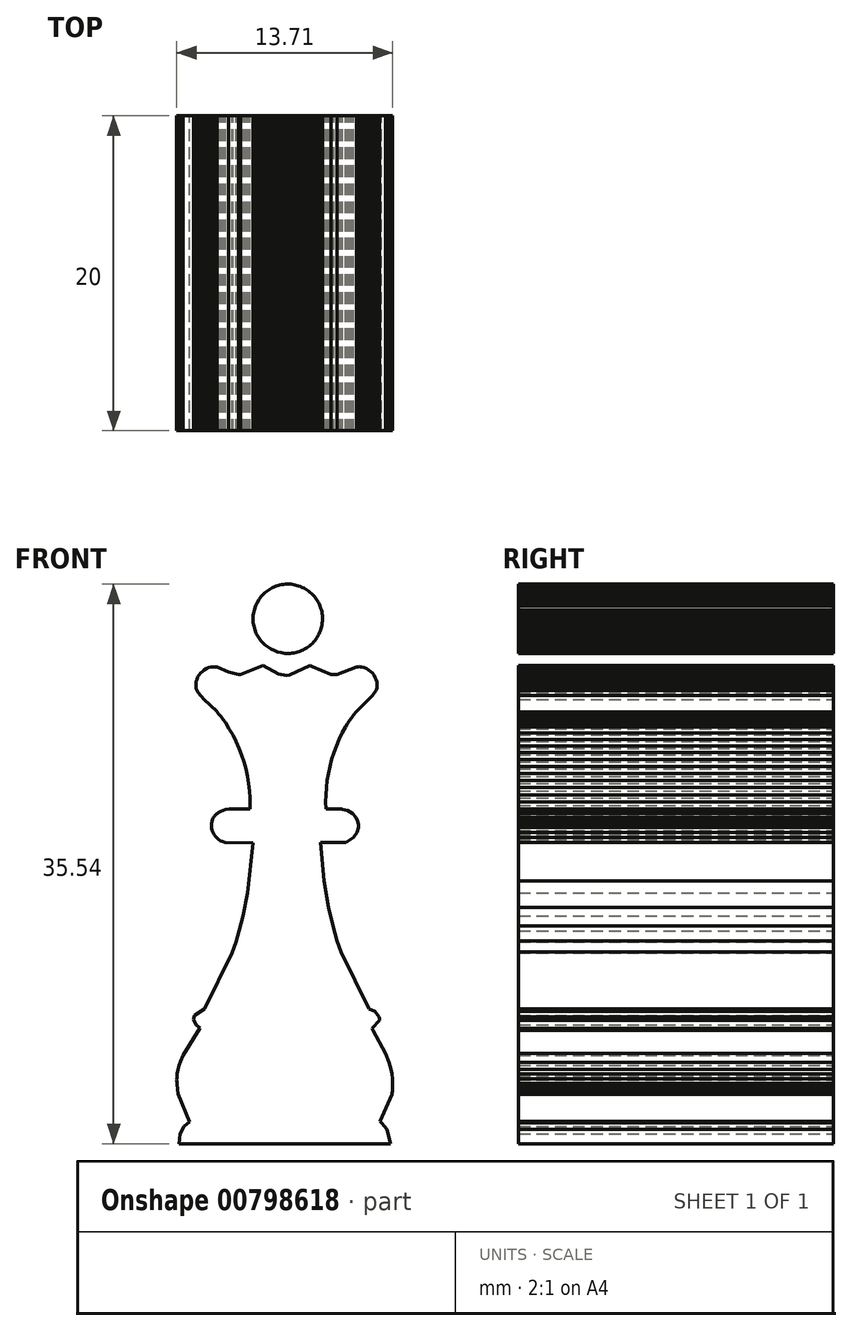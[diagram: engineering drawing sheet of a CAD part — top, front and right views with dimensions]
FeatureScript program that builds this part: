
annotation { "Feature Type Name" : "Feature", "Feature Type Description" : "" }
export const myFeature = defineFeature(function(context is Context, id is Id, definition is map)
    precondition{}
    {
        {
            var Q0;
            Q0=qCreatedBy(makeId("Front.planeOp"),FACE);
            var sketch = newSketch(context, id + "F0", { "sketchPlane" : qUnion([Q0])});
            skLineSegment(sketch, "E0", {"start": v(17.24, 35.4) * mm, "end": v(17.35, 35.45) * mm});
            skLineSegment(sketch, "E1", {"start": v(17.35, 35.45) * mm, "end": v(17.47, 35.48) * mm});
            skLineSegment(sketch, "E2", {"start": v(17.47, 35.48) * mm, "end": v(17.6, 35.51) * mm});
            skLineSegment(sketch, "E3", {"start": v(17.6, 35.51) * mm, "end": v(17.71, 35.53) * mm});
            skLineSegment(sketch, "E4", {"start": v(17.71, 35.53) * mm, "end": v(17.83, 35.54) * mm});
            skLineSegment(sketch, "E5", {"start": v(17.83, 35.54) * mm, "end": v(17.95, 35.54) * mm});
            skLineSegment(sketch, "E6", {"start": v(17.95, 35.54) * mm, "end": v(18.07, 35.54) * mm});
            skLineSegment(sketch, "E7", {"start": v(18.07, 35.54) * mm, "end": v(18.2, 35.53) * mm});
            skLineSegment(sketch, "E8", {"start": v(18.2, 35.53) * mm, "end": v(18.31, 35.52) * mm});
            skLineSegment(sketch, "E9", {"start": v(18.31, 35.52) * mm, "end": v(18.43, 35.5) * mm});
            skLineSegment(sketch, "E10", {"start": v(18.43, 35.5) * mm, "end": v(18.55, 35.46) * mm});
            skLineSegment(sketch, "E11", {"start": v(18.55, 35.46) * mm, "end": v(18.67, 35.43) * mm});
            skLineSegment(sketch, "E12", {"start": v(18.67, 35.43) * mm, "end": v(18.78, 35.39) * mm});
            skLineSegment(sketch, "E13", {"start": v(18.78, 35.39) * mm, "end": v(18.9, 35.34) * mm});
            skLineSegment(sketch, "E14", {"start": v(18.9, 35.34) * mm, "end": v(19, 35.29) * mm});
            skLineSegment(sketch, "E15", {"start": v(19, 35.29) * mm, "end": v(19.1, 35.23) * mm});
            skLineSegment(sketch, "E16", {"start": v(19.1, 35.23) * mm, "end": v(19.21, 35.16) * mm});
            skLineSegment(sketch, "E17", {"start": v(19.21, 35.16) * mm, "end": v(19.31, 35.1) * mm});
            skLineSegment(sketch, "E18", {"start": v(19.31, 35.1) * mm, "end": v(19.4, 35.02) * mm});
            skLineSegment(sketch, "E19", {"start": v(19.4, 35.02) * mm, "end": v(19.5, 34.94) * mm});
            skLineSegment(sketch, "E20", {"start": v(19.5, 34.94) * mm, "end": v(19.58, 34.85) * mm});
            skLineSegment(sketch, "E21", {"start": v(19.58, 34.85) * mm, "end": v(19.67, 34.77) * mm});
            skLineSegment(sketch, "E22", {"start": v(19.67, 34.77) * mm, "end": v(19.74, 34.67) * mm});
            skLineSegment(sketch, "E23", {"start": v(19.74, 34.67) * mm, "end": v(19.81, 34.57) * mm});
            skLineSegment(sketch, "E24", {"start": v(19.81, 34.57) * mm, "end": v(19.88, 34.47) * mm});
            skLineSegment(sketch, "E25", {"start": v(19.88, 34.47) * mm, "end": v(19.94, 34.37) * mm});
            skLineSegment(sketch, "E26", {"start": v(19.94, 34.37) * mm, "end": v(20, 34.26) * mm});
            skLineSegment(sketch, "E27", {"start": v(20, 34.26) * mm, "end": v(20.04, 34.14) * mm});
            skLineSegment(sketch, "E28", {"start": v(20.04, 34.14) * mm, "end": v(20.08, 34.02) * mm});
            skLineSegment(sketch, "E29", {"start": v(20.08, 34.02) * mm, "end": v(20.11, 33.9) * mm});
            skLineSegment(sketch, "E30", {"start": v(20.11, 33.9) * mm, "end": v(20.14, 33.79) * mm});
            skLineSegment(sketch, "E31", {"start": v(20.14, 33.79) * mm, "end": v(20.17, 33.67) * mm});
            skLineSegment(sketch, "E32", {"start": v(20.17, 33.67) * mm, "end": v(20.18, 33.55) * mm});
            skLineSegment(sketch, "E33", {"start": v(20.18, 33.55) * mm, "end": v(20.19, 33.43) * mm});
            skLineSegment(sketch, "E34", {"start": v(20.19, 33.43) * mm, "end": v(20.19, 33.3) * mm});
            skLineSegment(sketch, "E35", {"start": v(20.19, 33.3) * mm, "end": v(20.18, 33.18) * mm});
            skLineSegment(sketch, "E36", {"start": v(20.18, 33.18) * mm, "end": v(20.17, 33.06) * mm});
            skLineSegment(sketch, "E37", {"start": v(20.17, 33.06) * mm, "end": v(20.15, 32.94) * mm});
            skLineSegment(sketch, "E38", {"start": v(20.15, 32.94) * mm, "end": v(20.12, 32.83) * mm});
            skLineSegment(sketch, "E39", {"start": v(20.12, 32.83) * mm, "end": v(20.1, 32.7) * mm});
            skLineSegment(sketch, "E40", {"start": v(20.1, 32.7) * mm, "end": v(20.05, 32.6) * mm});
            skLineSegment(sketch, "E41", {"start": v(20.05, 32.6) * mm, "end": v(20, 32.48) * mm});
            skLineSegment(sketch, "E42", {"start": v(20, 32.48) * mm, "end": v(19.96, 32.37) * mm});
            skLineSegment(sketch, "E43", {"start": v(19.96, 32.37) * mm, "end": v(19.9, 32.26) * mm});
            skLineSegment(sketch, "E44", {"start": v(19.9, 32.26) * mm, "end": v(19.84, 32.16) * mm});
            skLineSegment(sketch, "E45", {"start": v(19.84, 32.16) * mm, "end": v(19.77, 32.06) * mm});
            skLineSegment(sketch, "E46", {"start": v(19.77, 32.06) * mm, "end": v(19.7, 31.96) * mm});
            skLineSegment(sketch, "E47", {"start": v(19.7, 31.96) * mm, "end": v(19.62, 31.87) * mm});
            skLineSegment(sketch, "E48", {"start": v(19.62, 31.87) * mm, "end": v(19.54, 31.78) * mm});
            skLineSegment(sketch, "E49", {"start": v(19.54, 31.78) * mm, "end": v(19.45, 31.7) * mm});
            skLineSegment(sketch, "E50", {"start": v(19.45, 31.7) * mm, "end": v(19.36, 31.62) * mm});
            skLineSegment(sketch, "E51", {"start": v(19.36, 31.62) * mm, "end": v(19.26, 31.54) * mm});
            skLineSegment(sketch, "E52", {"start": v(19.26, 31.54) * mm, "end": v(19.16, 31.48) * mm});
            skLineSegment(sketch, "E53", {"start": v(19.16, 31.48) * mm, "end": v(19.06, 31.42) * mm});
            skLineSegment(sketch, "E54", {"start": v(19.06, 31.42) * mm, "end": v(18.95, 31.36) * mm});
            skLineSegment(sketch, "E55", {"start": v(18.95, 31.36) * mm, "end": v(18.84, 31.31) * mm});
            skLineSegment(sketch, "E56", {"start": v(18.84, 31.31) * mm, "end": v(18.72, 31.27) * mm});
            skLineSegment(sketch, "E57", {"start": v(18.72, 31.27) * mm, "end": v(18.6, 31.23) * mm});
            skLineSegment(sketch, "E58", {"start": v(18.6, 31.23) * mm, "end": v(18.5, 31.2) * mm});
            skLineSegment(sketch, "E59", {"start": v(18.5, 31.2) * mm, "end": v(18.38, 31.18) * mm});
            skLineSegment(sketch, "E60", {"start": v(18.38, 31.18) * mm, "end": v(18.26, 31.16) * mm});
            skLineSegment(sketch, "E61", {"start": v(18.26, 31.16) * mm, "end": v(18.15, 31.15) * mm});
            skLineSegment(sketch, "E62", {"start": v(18.15, 31.15) * mm, "end": v(18.03, 31.14) * mm});
            skLineSegment(sketch, "E63", {"start": v(18.03, 31.14) * mm, "end": v(17.91, 31.14) * mm});
            skLineSegment(sketch, "E64", {"start": v(17.91, 31.14) * mm, "end": v(17.8, 31.15) * mm});
            skLineSegment(sketch, "E65", {"start": v(17.8, 31.15) * mm, "end": v(17.57, 31.18) * mm});
            skLineSegment(sketch, "E66", {"start": v(17.57, 31.18) * mm, "end": v(17.34, 31.24) * mm});
            skLineSegment(sketch, "E67", {"start": v(17.34, 31.24) * mm, "end": v(17.13, 31.32) * mm});
            skLineSegment(sketch, "E68", {"start": v(17.13, 31.32) * mm, "end": v(16.92, 31.42) * mm});
            skLineSegment(sketch, "E69", {"start": v(16.92, 31.42) * mm, "end": v(16.72, 31.54) * mm});
            skLineSegment(sketch, "E70", {"start": v(16.72, 31.54) * mm, "end": v(16.54, 31.69) * mm});
            skLineSegment(sketch, "E71", {"start": v(16.54, 31.69) * mm, "end": v(16.37, 31.85) * mm});
            skLineSegment(sketch, "E72", {"start": v(16.37, 31.85) * mm, "end": v(16.29, 31.93) * mm});
            skLineSegment(sketch, "E73", {"start": v(16.29, 31.93) * mm, "end": v(16.22, 32.02) * mm});
            skLineSegment(sketch, "E74", {"start": v(16.22, 32.02) * mm, "end": v(16.15, 32.12) * mm});
            skLineSegment(sketch, "E75", {"start": v(16.15, 32.12) * mm, "end": v(16.09, 32.21) * mm});
            skLineSegment(sketch, "E76", {"start": v(16.09, 32.21) * mm, "end": v(16.03, 32.31) * mm});
            skLineSegment(sketch, "E77", {"start": v(16.03, 32.31) * mm, "end": v(15.98, 32.42) * mm});
            skLineSegment(sketch, "E78", {"start": v(15.98, 32.42) * mm, "end": v(15.93, 32.53) * mm});
            skLineSegment(sketch, "E79", {"start": v(15.93, 32.53) * mm, "end": v(15.9, 32.64) * mm});
            skLineSegment(sketch, "E80", {"start": v(15.9, 32.64) * mm, "end": v(15.86, 32.75) * mm});
            skLineSegment(sketch, "E81", {"start": v(15.86, 32.75) * mm, "end": v(15.83, 32.87) * mm});
            skLineSegment(sketch, "E82", {"start": v(15.83, 32.87) * mm, "end": v(15.8, 32.98) * mm});
            skLineSegment(sketch, "E83", {"start": v(15.8, 32.98) * mm, "end": v(15.79, 33.1) * mm});
            skLineSegment(sketch, "E84", {"start": v(15.79, 33.1) * mm, "end": v(15.78, 33.22) * mm});
            skLineSegment(sketch, "E85", {"start": v(15.78, 33.22) * mm, "end": v(15.77, 33.34) * mm});
            skLineSegment(sketch, "E86", {"start": v(15.77, 33.34) * mm, "end": v(15.78, 33.45) * mm});
            skLineSegment(sketch, "E87", {"start": v(15.78, 33.45) * mm, "end": v(15.79, 33.57) * mm});
            skLineSegment(sketch, "E88", {"start": v(15.79, 33.57) * mm, "end": v(15.8, 33.68) * mm});
            skLineSegment(sketch, "E89", {"start": v(15.8, 33.68) * mm, "end": v(15.86, 33.91) * mm});
            skLineSegment(sketch, "E90", {"start": v(15.86, 33.91) * mm, "end": v(15.93, 34.14) * mm});
            skLineSegment(sketch, "E91", {"start": v(15.93, 34.14) * mm, "end": v(16.03, 34.35) * mm});
            skLineSegment(sketch, "E92", {"start": v(16.03, 34.35) * mm, "end": v(16.15, 34.55) * mm});
            skLineSegment(sketch, "E93", {"start": v(16.15, 34.55) * mm, "end": v(16.29, 34.74) * mm});
            skLineSegment(sketch, "E94", {"start": v(16.29, 34.74) * mm, "end": v(16.44, 34.91) * mm});
            skLineSegment(sketch, "E95", {"start": v(16.44, 34.91) * mm, "end": v(16.53, 35) * mm});
            skLineSegment(sketch, "E96", {"start": v(16.53, 35) * mm, "end": v(16.62, 35.07) * mm});
            skLineSegment(sketch, "E97", {"start": v(16.62, 35.07) * mm, "end": v(16.71, 35.14) * mm});
            skLineSegment(sketch, "E98", {"start": v(16.71, 35.14) * mm, "end": v(16.81, 35.2) * mm});
            skLineSegment(sketch, "E99", {"start": v(16.81, 35.2) * mm, "end": v(16.91, 35.27) * mm});
            skLineSegment(sketch, "E100", {"start": v(16.91, 35.27) * mm, "end": v(17.02, 35.32) * mm});
            skLineSegment(sketch, "E101", {"start": v(17.02, 35.32) * mm, "end": v(17.12, 35.37) * mm});
            skLineSegment(sketch, "E102", {"start": v(17.12, 35.37) * mm, "end": v(17.24, 35.4) * mm});
            skLineSegment(sketch, "E103", {"start": v(12.17, 28.9) * mm, "end": v(12.15, 28.97) * mm});
            skLineSegment(sketch, "E104", {"start": v(12.15, 28.97) * mm, "end": v(12.14, 29.05) * mm});
            skLineSegment(sketch, "E105", {"start": v(12.14, 29.05) * mm, "end": v(12.14, 29.2) * mm});
            skLineSegment(sketch, "E106", {"start": v(12.14, 29.2) * mm, "end": v(12.16, 29.35) * mm});
            skLineSegment(sketch, "E107", {"start": v(12.16, 29.35) * mm, "end": v(12.2, 29.5) * mm});
            skLineSegment(sketch, "E108", {"start": v(12.2, 29.5) * mm, "end": v(12.27, 29.64) * mm});
            skLineSegment(sketch, "E109", {"start": v(12.27, 29.64) * mm, "end": v(12.35, 29.77) * mm});
            skLineSegment(sketch, "E110", {"start": v(12.35, 29.77) * mm, "end": v(12.44, 29.9) * mm});
            skLineSegment(sketch, "E111", {"start": v(12.44, 29.9) * mm, "end": v(12.55, 30) * mm});
            skLineSegment(sketch, "E112", {"start": v(12.55, 30) * mm, "end": v(12.68, 30.1) * mm});
            skLineSegment(sketch, "E113", {"start": v(12.68, 30.1) * mm, "end": v(12.8, 30.17) * mm});
            skLineSegment(sketch, "E114", {"start": v(12.8, 30.17) * mm, "end": v(12.95, 30.23) * mm});
            skLineSegment(sketch, "E115", {"start": v(12.95, 30.23) * mm, "end": v(13.1, 30.27) * mm});
            skLineSegment(sketch, "E116", {"start": v(13.1, 30.27) * mm, "end": v(13.25, 30.3) * mm});
            skLineSegment(sketch, "E117", {"start": v(13.25, 30.3) * mm, "end": v(13.4, 30.29) * mm});
            skLineSegment(sketch, "E118", {"start": v(13.4, 30.29) * mm, "end": v(13.48, 30.28) * mm});
            skLineSegment(sketch, "E119", {"start": v(13.48, 30.28) * mm, "end": v(14.23, 29.95) * mm});
            skLineSegment(sketch, "E120", {"start": v(14.23, 29.95) * mm, "end": v(14.87, 29.8) * mm});
            skLineSegment(sketch, "E121", {"start": v(14.87, 29.8) * mm, "end": v(14.98, 29.8) * mm});
            skLineSegment(sketch, "E122", {"start": v(14.98, 29.8) * mm, "end": v(16.4, 30.37) * mm});
            skLineSegment(sketch, "E123", {"start": v(16.4, 30.37) * mm, "end": v(17.4, 29.82) * mm});
            skLineSegment(sketch, "E124", {"start": v(17.4, 29.82) * mm, "end": v(17.91, 29.75) * mm});
            skLineSegment(sketch, "E125", {"start": v(17.91, 29.75) * mm, "end": v(18.08, 29.76) * mm});
            skLineSegment(sketch, "E126", {"start": v(18.08, 29.76) * mm, "end": v(19.4, 30.37) * mm});
            skLineSegment(sketch, "E127", {"start": v(19.4, 30.37) * mm, "end": v(19.51, 30.3) * mm});
            skLineSegment(sketch, "E128", {"start": v(19.51, 30.3) * mm, "end": v(20.72, 29.8) * mm});
            skLineSegment(sketch, "E129", {"start": v(20.72, 29.8) * mm, "end": v(21.1, 29.81) * mm});
            skLineSegment(sketch, "E130", {"start": v(21.1, 29.81) * mm, "end": v(22.36, 30.28) * mm});
            skLineSegment(sketch, "E131", {"start": v(22.36, 30.28) * mm, "end": v(22.44, 30.3) * mm});
            skLineSegment(sketch, "E132", {"start": v(22.44, 30.3) * mm, "end": v(22.52, 30.3) * mm});
            skLineSegment(sketch, "E133", {"start": v(22.52, 30.3) * mm, "end": v(22.6, 30.29) * mm});
            skLineSegment(sketch, "E134", {"start": v(22.6, 30.29) * mm, "end": v(22.68, 30.28) * mm});
            skLineSegment(sketch, "E135", {"start": v(22.68, 30.28) * mm, "end": v(22.83, 30.24) * mm});
            skLineSegment(sketch, "E136", {"start": v(22.83, 30.24) * mm, "end": v(22.97, 30.18) * mm});
            skLineSegment(sketch, "E137", {"start": v(22.97, 30.18) * mm, "end": v(23.11, 30.1) * mm});
            skLineSegment(sketch, "E138", {"start": v(23.11, 30.1) * mm, "end": v(23.24, 30) * mm});
            skLineSegment(sketch, "E139", {"start": v(23.24, 30) * mm, "end": v(23.35, 29.89) * mm});
            skLineSegment(sketch, "E140", {"start": v(23.35, 29.89) * mm, "end": v(23.45, 29.76) * mm});
            skLineSegment(sketch, "E141", {"start": v(23.45, 29.76) * mm, "end": v(23.53, 29.63) * mm});
            skLineSegment(sketch, "E142", {"start": v(23.53, 29.63) * mm, "end": v(23.6, 29.48) * mm});
            skLineSegment(sketch, "E143", {"start": v(23.6, 29.48) * mm, "end": v(23.63, 29.33) * mm});
            skLineSegment(sketch, "E144", {"start": v(23.63, 29.33) * mm, "end": v(23.65, 29.18) * mm});
            skLineSegment(sketch, "E145", {"start": v(23.65, 29.18) * mm, "end": v(23.65, 29.1) * mm});
            skLineSegment(sketch, "E146", {"start": v(23.65, 29.1) * mm, "end": v(23.65, 29.02) * mm});
            skLineSegment(sketch, "E147", {"start": v(23.65, 29.02) * mm, "end": v(23.63, 28.94) * mm});
            skLineSegment(sketch, "E148", {"start": v(23.63, 28.94) * mm, "end": v(23.61, 28.86) * mm});
            skLineSegment(sketch, "E149", {"start": v(23.61, 28.86) * mm, "end": v(23.59, 28.79) * mm});
            skLineSegment(sketch, "E150", {"start": v(23.59, 28.79) * mm, "end": v(23.38, 28.46) * mm});
            skLineSegment(sketch, "E151", {"start": v(23.38, 28.46) * mm, "end": v(22.3, 27.42) * mm});
            skLineSegment(sketch, "E152", {"start": v(22.3, 27.42) * mm, "end": v(22.17, 27.24) * mm});
            skLineSegment(sketch, "E153", {"start": v(22.17, 27.24) * mm, "end": v(22.03, 27.05) * mm});
            skLineSegment(sketch, "E154", {"start": v(22.03, 27.05) * mm, "end": v(21.9, 26.87) * mm});
            skLineSegment(sketch, "E155", {"start": v(21.9, 26.87) * mm, "end": v(21.78, 26.68) * mm});
            skLineSegment(sketch, "E156", {"start": v(21.78, 26.68) * mm, "end": v(21.66, 26.48) * mm});
            skLineSegment(sketch, "E157", {"start": v(21.66, 26.48) * mm, "end": v(21.44, 26.08) * mm});
            skLineSegment(sketch, "E158", {"start": v(21.44, 26.08) * mm, "end": v(21.24, 25.68) * mm});
            skLineSegment(sketch, "E159", {"start": v(21.24, 25.68) * mm, "end": v(21.06, 25.26) * mm});
            skLineSegment(sketch, "E160", {"start": v(21.06, 25.26) * mm, "end": v(20.9, 24.83) * mm});
            skLineSegment(sketch, "E161", {"start": v(20.9, 24.83) * mm, "end": v(20.77, 24.4) * mm});
            skLineSegment(sketch, "E162", {"start": v(20.77, 24.4) * mm, "end": v(20.65, 23.96) * mm});
            skLineSegment(sketch, "E163", {"start": v(20.65, 23.96) * mm, "end": v(20.56, 23.51) * mm});
            skLineSegment(sketch, "E164", {"start": v(20.56, 23.51) * mm, "end": v(20.49, 23.06) * mm});
            skLineSegment(sketch, "E165", {"start": v(20.49, 23.06) * mm, "end": v(20.43, 22.61) * mm});
            skLineSegment(sketch, "E166", {"start": v(20.43, 22.61) * mm, "end": v(20.4, 22.16) * mm});
            skLineSegment(sketch, "E167", {"start": v(20.4, 22.16) * mm, "end": v(20.4, 21.7) * mm});
            skLineSegment(sketch, "E168", {"start": v(20.4, 21.7) * mm, "end": v(20.4, 21.25) * mm});
            skLineSegment(sketch, "E169", {"start": v(20.4, 21.25) * mm, "end": v(21.4, 21.25) * mm});
            skLineSegment(sketch, "E170", {"start": v(21.4, 21.25) * mm, "end": v(21.46, 21.24) * mm});
            skLineSegment(sketch, "E171", {"start": v(21.46, 21.24) * mm, "end": v(21.77, 21.17) * mm});
            skLineSegment(sketch, "E172", {"start": v(21.77, 21.17) * mm, "end": v(22.1, 20.97) * mm});
            skLineSegment(sketch, "E173", {"start": v(22.1, 20.97) * mm, "end": v(22.3, 20.73) * mm});
            skLineSegment(sketch, "E174", {"start": v(22.3, 20.73) * mm, "end": v(22.42, 20.49) * mm});
            skLineSegment(sketch, "E175", {"start": v(22.42, 20.49) * mm, "end": v(22.46, 20.28) * mm});
            skLineSegment(sketch, "E176", {"start": v(22.46, 20.28) * mm, "end": v(22.46, 20.07) * mm});
            skLineSegment(sketch, "E177", {"start": v(22.46, 20.07) * mm, "end": v(22.38, 19.78) * mm});
            skLineSegment(sketch, "E178", {"start": v(22.38, 19.78) * mm, "end": v(22.15, 19.45) * mm});
            skLineSegment(sketch, "E179", {"start": v(22.15, 19.45) * mm, "end": v(21.69, 19.15) * mm});
            skLineSegment(sketch, "E180", {"start": v(21.69, 19.15) * mm, "end": v(20.06, 19.13) * mm});
            skLineSegment(sketch, "E181", {"start": v(20.06, 19.13) * mm, "end": v(20.29, 16.7) * mm});
            skLineSegment(sketch, "E182", {"start": v(20.29, 16.7) * mm, "end": v(20.56, 15) * mm});
            skLineSegment(sketch, "E183", {"start": v(20.56, 15) * mm, "end": v(20.84, 13.82) * mm});
            skLineSegment(sketch, "E184", {"start": v(20.84, 13.82) * mm, "end": v(21.12, 12.88) * mm});
            skLineSegment(sketch, "E185", {"start": v(21.12, 12.88) * mm, "end": v(21.37, 12.19) * mm});
            skLineSegment(sketch, "E186", {"start": v(21.37, 12.19) * mm, "end": v(23.13, 8.56) * mm});
            skLineSegment(sketch, "E187", {"start": v(23.13, 8.56) * mm, "end": v(23.52, 8.4) * mm});
            skLineSegment(sketch, "E188", {"start": v(23.52, 8.4) * mm, "end": v(23.79, 8.04) * mm});
            skLineSegment(sketch, "E189", {"start": v(23.79, 8.04) * mm, "end": v(23.8, 7.97) * mm});
            skLineSegment(sketch, "E190", {"start": v(23.8, 7.97) * mm, "end": v(23.8, 7.82) * mm});
            skLineSegment(sketch, "E191", {"start": v(23.8, 7.82) * mm, "end": v(23.33, 7.34) * mm});
            skLineSegment(sketch, "E192", {"start": v(23.33, 7.34) * mm, "end": v(23.4, 7.2) * mm});
            skLineSegment(sketch, "E193", {"start": v(23.4, 7.2) * mm, "end": v(24.2, 5.72) * mm});
            skLineSegment(sketch, "E194", {"start": v(24.2, 5.72) * mm, "end": v(24.4, 5.15) * mm});
            skLineSegment(sketch, "E195", {"start": v(24.4, 5.15) * mm, "end": v(24.53, 4.71) * mm});
            skLineSegment(sketch, "E196", {"start": v(24.53, 4.71) * mm, "end": v(24.59, 4.42) * mm});
            skLineSegment(sketch, "E197", {"start": v(24.59, 4.42) * mm, "end": v(24.63, 4.12) * mm});
            skLineSegment(sketch, "E198", {"start": v(24.63, 4.12) * mm, "end": v(24.64, 3.82) * mm});
            skLineSegment(sketch, "E199", {"start": v(24.64, 3.82) * mm, "end": v(24.64, 3.66) * mm});
            skLineSegment(sketch, "E200", {"start": v(24.64, 3.66) * mm, "end": v(24.63, 3.5) * mm});
            skLineSegment(sketch, "E201", {"start": v(24.63, 3.5) * mm, "end": v(24.62, 3.35) * mm});
            skLineSegment(sketch, "E202", {"start": v(24.62, 3.35) * mm, "end": v(24.6, 3.2) * mm});
            skLineSegment(sketch, "E203", {"start": v(24.6, 3.2) * mm, "end": v(24.6, 3.13) * mm});
            skLineSegment(sketch, "E204", {"start": v(24.6, 3.13) * mm, "end": v(23.85, 1.4) * mm});
            skLineSegment(sketch, "E205", {"start": v(23.85, 1.4) * mm, "end": v(23.94, 1.33) * mm});
            skLineSegment(sketch, "E206", {"start": v(23.94, 1.33) * mm, "end": v(24.28, 0.9) * mm});
            skLineSegment(sketch, "E207", {"start": v(24.28, 0.9) * mm, "end": v(24.5, 0) * mm});
            skLineSegment(sketch, "E208", {"start": v(24.5, 0) * mm, "end": v(11.06, 0) * mm});
            skLineSegment(sketch, "E209", {"start": v(11.06, 0) * mm, "end": v(11.14, 0.6) * mm});
            skLineSegment(sketch, "E210", {"start": v(11.14, 0.6) * mm, "end": v(11.4, 1.09) * mm});
            skLineSegment(sketch, "E211", {"start": v(11.4, 1.09) * mm, "end": v(11.73, 1.39) * mm});
            skLineSegment(sketch, "E212", {"start": v(11.73, 1.39) * mm, "end": v(11, 3.15) * mm});
            skLineSegment(sketch, "E213", {"start": v(11, 3.15) * mm, "end": v(10.95, 3.76) * mm});
            skLineSegment(sketch, "E214", {"start": v(10.95, 3.76) * mm, "end": v(10.94, 3.9) * mm});
            skLineSegment(sketch, "E215", {"start": v(10.94, 3.9) * mm, "end": v(10.93, 4.04) * mm});
            skLineSegment(sketch, "E216", {"start": v(10.93, 4.04) * mm, "end": v(10.94, 4.18) * mm});
            skLineSegment(sketch, "E217", {"start": v(10.94, 4.18) * mm, "end": v(10.95, 4.31) * mm});
            skLineSegment(sketch, "E218", {"start": v(10.95, 4.31) * mm, "end": v(10.96, 4.45) * mm});
            skLineSegment(sketch, "E219", {"start": v(10.96, 4.45) * mm, "end": v(11.02, 4.7) * mm});
            skLineSegment(sketch, "E220", {"start": v(11.02, 4.7) * mm, "end": v(11.09, 4.97) * mm});
            skLineSegment(sketch, "E221", {"start": v(11.09, 4.97) * mm, "end": v(11.18, 5.22) * mm});
            skLineSegment(sketch, "E222", {"start": v(11.18, 5.22) * mm, "end": v(11.35, 5.6) * mm});
            skLineSegment(sketch, "E223", {"start": v(11.35, 5.6) * mm, "end": v(12.4, 7.36) * mm});
            skLineSegment(sketch, "E224", {"start": v(12.4, 7.36) * mm, "end": v(12.17, 7.55) * mm});
            skLineSegment(sketch, "E225", {"start": v(12.17, 7.55) * mm, "end": v(11.98, 7.9) * mm});
            skLineSegment(sketch, "E226", {"start": v(11.98, 7.9) * mm, "end": v(12.02, 8.05) * mm});
            skLineSegment(sketch, "E227", {"start": v(12.02, 8.05) * mm, "end": v(12.05, 8.15) * mm});
            skLineSegment(sketch, "E228", {"start": v(12.05, 8.15) * mm, "end": v(12.7, 8.56) * mm});
            skLineSegment(sketch, "E229", {"start": v(12.7, 8.56) * mm, "end": v(14.43, 12.1) * mm});
            skLineSegment(sketch, "E230", {"start": v(14.43, 12.1) * mm, "end": v(14.68, 12.8) * mm});
            skLineSegment(sketch, "E231", {"start": v(14.68, 12.8) * mm, "end": v(14.9, 13.51) * mm});
            skLineSegment(sketch, "E232", {"start": v(14.9, 13.51) * mm, "end": v(15.14, 14.46) * mm});
            skLineSegment(sketch, "E233", {"start": v(15.14, 14.46) * mm, "end": v(15.42, 15.92) * mm});
            skLineSegment(sketch, "E234", {"start": v(15.42, 15.92) * mm, "end": v(15.77, 19.1) * mm});
            skLineSegment(sketch, "E235", {"start": v(15.77, 19.1) * mm, "end": v(14, 19.14) * mm});
            skLineSegment(sketch, "E236", {"start": v(14, 19.14) * mm, "end": v(13.85, 19.18) * mm});
            skLineSegment(sketch, "E237", {"start": v(13.85, 19.18) * mm, "end": v(13.72, 19.24) * mm});
            skLineSegment(sketch, "E238", {"start": v(13.72, 19.24) * mm, "end": v(13.6, 19.32) * mm});
            skLineSegment(sketch, "E239", {"start": v(13.6, 19.32) * mm, "end": v(13.48, 19.41) * mm});
            skLineSegment(sketch, "E240", {"start": v(13.48, 19.41) * mm, "end": v(13.38, 19.52) * mm});
            skLineSegment(sketch, "E241", {"start": v(13.38, 19.52) * mm, "end": v(13.3, 19.64) * mm});
            skLineSegment(sketch, "E242", {"start": v(13.3, 19.64) * mm, "end": v(13.23, 19.77) * mm});
            skLineSegment(sketch, "E243", {"start": v(13.23, 19.77) * mm, "end": v(13.18, 19.9) * mm});
            skLineSegment(sketch, "E244", {"start": v(13.18, 19.9) * mm, "end": v(13.14, 20.05) * mm});
            skLineSegment(sketch, "E245", {"start": v(13.14, 20.05) * mm, "end": v(13.13, 20.2) * mm});
            skLineSegment(sketch, "E246", {"start": v(13.13, 20.2) * mm, "end": v(13.13, 20.33) * mm});
            skLineSegment(sketch, "E247", {"start": v(13.13, 20.33) * mm, "end": v(13.16, 20.48) * mm});
            skLineSegment(sketch, "E248", {"start": v(13.16, 20.48) * mm, "end": v(13.22, 20.61) * mm});
            skLineSegment(sketch, "E249", {"start": v(13.22, 20.61) * mm, "end": v(13.25, 20.68) * mm});
            skLineSegment(sketch, "E250", {"start": v(13.25, 20.68) * mm, "end": v(13.3, 20.74) * mm});
            skLineSegment(sketch, "E251", {"start": v(13.3, 20.74) * mm, "end": v(13.34, 20.8) * mm});
            skLineSegment(sketch, "E252", {"start": v(13.34, 20.8) * mm, "end": v(13.4, 20.87) * mm});
            skLineSegment(sketch, "E253", {"start": v(13.4, 20.87) * mm, "end": v(13.46, 20.93) * mm});
            skLineSegment(sketch, "E254", {"start": v(13.46, 20.93) * mm, "end": v(13.52, 20.99) * mm});
            skLineSegment(sketch, "E255", {"start": v(13.52, 20.99) * mm, "end": v(13.58, 21.04) * mm});
            skLineSegment(sketch, "E256", {"start": v(13.58, 21.04) * mm, "end": v(13.72, 21.11) * mm});
            skLineSegment(sketch, "E257", {"start": v(13.72, 21.11) * mm, "end": v(13.87, 21.17) * mm});
            skLineSegment(sketch, "E258", {"start": v(13.87, 21.17) * mm, "end": v(14.02, 21.22) * mm});
            skLineSegment(sketch, "E259", {"start": v(14.02, 21.22) * mm, "end": v(14.26, 21.25) * mm});
            skLineSegment(sketch, "E260", {"start": v(14.26, 21.25) * mm, "end": v(15.57, 21.25) * mm});
            skLineSegment(sketch, "E261", {"start": v(15.57, 21.25) * mm, "end": v(15.58, 21.48) * mm});
            skLineSegment(sketch, "E262", {"start": v(15.58, 21.48) * mm, "end": v(15.58, 21.95) * mm});
            skLineSegment(sketch, "E263", {"start": v(15.58, 21.95) * mm, "end": v(15.55, 22.4) * mm});
            skLineSegment(sketch, "E264", {"start": v(15.55, 22.4) * mm, "end": v(15.5, 22.87) * mm});
            skLineSegment(sketch, "E265", {"start": v(15.5, 22.87) * mm, "end": v(15.42, 23.33) * mm});
            skLineSegment(sketch, "E266", {"start": v(15.42, 23.33) * mm, "end": v(15.32, 23.78) * mm});
            skLineSegment(sketch, "E267", {"start": v(15.32, 23.78) * mm, "end": v(15.2, 24.23) * mm});
            skLineSegment(sketch, "E268", {"start": v(15.2, 24.23) * mm, "end": v(15.06, 24.68) * mm});
            skLineSegment(sketch, "E269", {"start": v(15.06, 24.68) * mm, "end": v(14.9, 25.11) * mm});
            skLineSegment(sketch, "E270", {"start": v(14.9, 25.11) * mm, "end": v(14.7, 25.54) * mm});
            skLineSegment(sketch, "E271", {"start": v(14.7, 25.54) * mm, "end": v(14.5, 25.95) * mm});
            skLineSegment(sketch, "E272", {"start": v(14.5, 25.95) * mm, "end": v(14.27, 26.35) * mm});
            skLineSegment(sketch, "E273", {"start": v(14.27, 26.35) * mm, "end": v(14.01, 26.74) * mm});
            skLineSegment(sketch, "E274", {"start": v(14.01, 26.74) * mm, "end": v(13.88, 26.93) * mm});
            skLineSegment(sketch, "E275", {"start": v(13.88, 26.93) * mm, "end": v(13.74, 27.12) * mm});
            skLineSegment(sketch, "E276", {"start": v(13.74, 27.12) * mm, "end": v(13.6, 27.3) * mm});
            skLineSegment(sketch, "E277", {"start": v(13.6, 27.3) * mm, "end": v(13.45, 27.48) * mm});
            skLineSegment(sketch, "E278", {"start": v(13.45, 27.48) * mm, "end": v(12.67, 28.2) * mm});
            skLineSegment(sketch, "E279", {"start": v(12.67, 28.2) * mm, "end": v(12.28, 28.65) * mm});
            skLineSegment(sketch, "E280", {"start": v(12.28, 28.65) * mm, "end": v(12.17, 28.9) * mm});
            skSolve(sketch);
        }
        {
            var Q0;
            Q0 = qSketchRegion(id + "F0", true);
            extrude(context, id + "F1", {"entities" : qUnion([Q0]), "depth" : 20 * mm, "offsetDistance" : 25 * mm});
        }
    });
